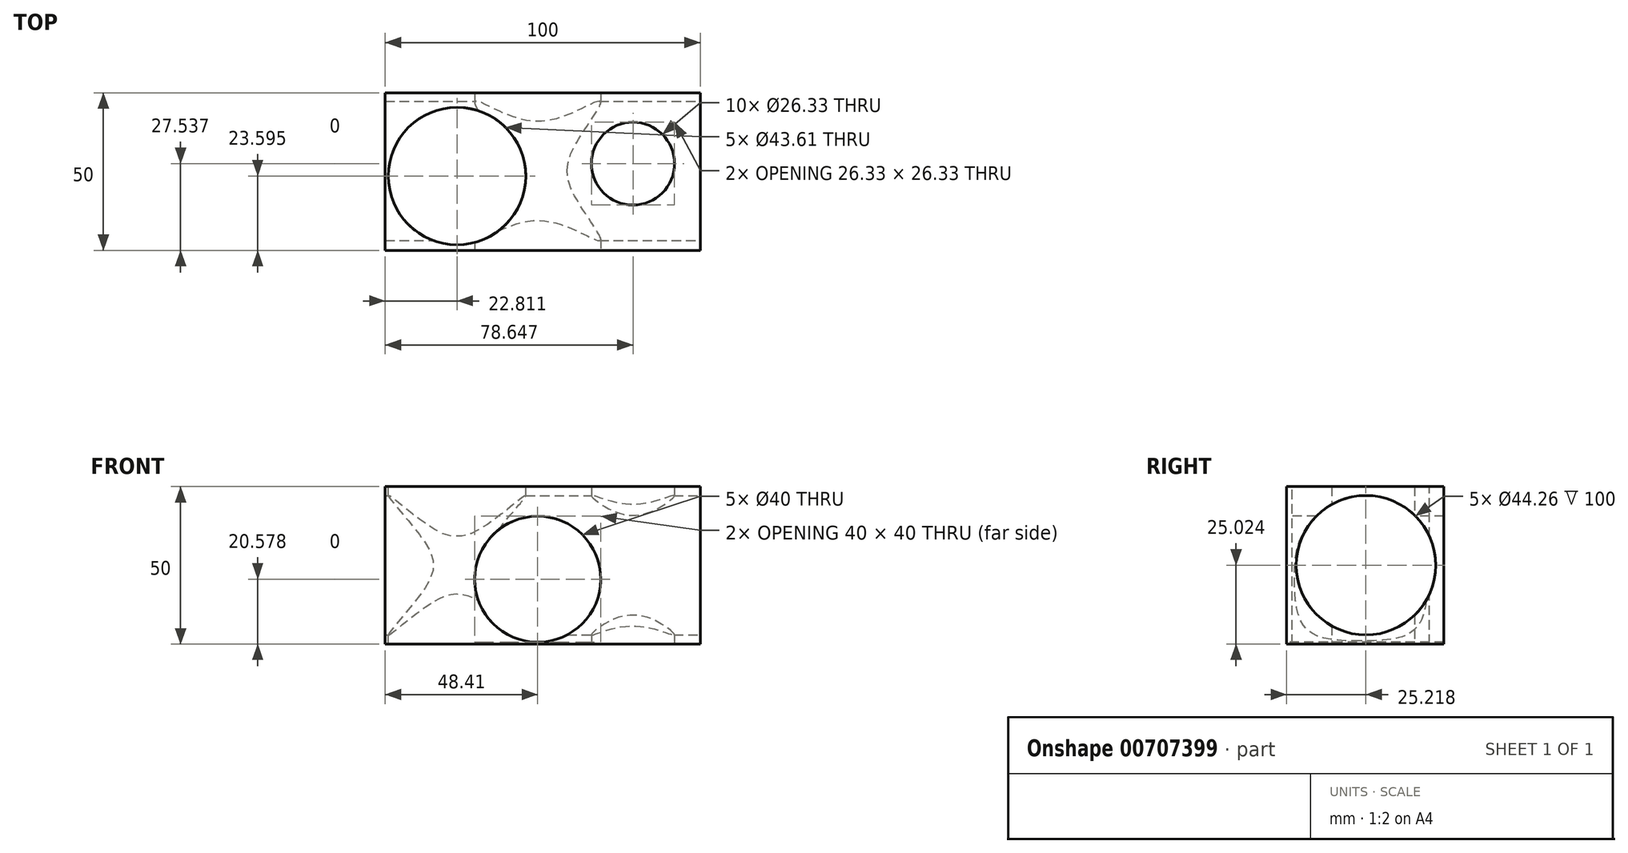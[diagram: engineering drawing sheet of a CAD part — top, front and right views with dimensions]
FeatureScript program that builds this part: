
annotation { "Feature Type Name" : "Feature", "Feature Type Description" : "" }
export const myFeature = defineFeature(function(context is Context, id is Id, definition is map)
    precondition{}
    {
        {
            var Q0;
            Q0=qCreatedBy(makeId("Top.planeOp"),FACE);
            var sketch = newSketch(context, id + "F0", { "sketchPlane" : qUnion([Q0])});
            skLineSegment(sketch, "E0.bottom", {"start": v(-48.41, 7.4) * mm, "end": v(51.59, 7.4) * mm});
            skLineSegment(sketch, "E0.top", {"start": v(-48.41, -42.6) * mm, "end": v(51.59, -42.6) * mm});
            skLineSegment(sketch, "E0.left", {"start": v(-48.41, 7.4) * mm, "end": v(-48.41, -42.6) * mm});
            skLineSegment(sketch, "E0.right", {"start": v(51.59, 7.4) * mm, "end": v(51.59, -42.6) * mm});
            skSolve(sketch);
        }
        {
            var Q0;
            Q0=makeQuery(id+"F0.imprint","IMPRINT",FACE,{"disambiguationData":[TD([[makeQuery(id+"F0.imprint","IMPRINT",EDGE,{"derivedFrom":sQuery(id+"F0.wireOp",EDGE,"E0.bottom")}),-1.0]])]});
            extrude(context, id + "F1", {"entities" : qUnion([Q0]), "depth" : 50 * mm, "offsetDistance" : 25 * mm});
        }
        {
            var Q0;
            Q0=makeQuery(id+"F1.opExtrude","SWEPT_FACE",FACE,{"disambiguationData":[OSD([sQuery(id+"F0.wireOp",EDGE,"E0.top")])]});
            var sketch = newSketch(context, id + "F2", { "sketchPlane" : qUnion([Q0])});
            skCircle(sketch, "E1", {"center": v(0, 20.58) * mm, "radius": 20 * mm});
            skSolve(sketch);
        }
        {
            var Q0;
            Q0=makeQuery(id+"F2.imprint","IMPRINT",FACE,{"disambiguationData":[TD([[makeQuery(id+"F2.imprint","IMPRINT",EDGE,{"derivedFrom":sQuery(id+"F2.wireOp",EDGE,"E1")}),1.0]])]});
            extrude(context, id + "F3", {"entities" : qUnion([Q0]), "operationType" : NewBodyOperationType.REMOVE, "endBound" : BoundingType.UP_TO_NEXT, "oppositeDirection" : true, "depth" : 50 * mm, "offsetDistance" : 25 * mm});
        }
        {
            var Q0;
            Q0=makeQuery(id+"F1.opExtrude","CAP_FACE",FACE,{"disambiguationData":[OSD([sQuery(id+"F0.wireOp",EDGE,"E0.bottom"),sQuery(id+"F0.wireOp",EDGE,"E0.top"),sQuery(id+"F0.wireOp",EDGE,"E0.left"),sQuery(id+"F0.wireOp",EDGE,"E0.right")])],"isStart":true});
            var sketch = newSketch(context, id + "F4", { "sketchPlane" : qUnion([Q0])});
            skCircle(sketch, "E2", {"center": v(30.24, 15.06) * mm, "radius": 13.17 * mm});
            skSolve(sketch);
        }
        {
            var Q0;
            Q0=makeQuery(id+"F4.imprint","IMPRINT",FACE,{"disambiguationData":[TD([[makeQuery(id+"F4.imprint","IMPRINT",EDGE,{"derivedFrom":sQuery(id+"F4.wireOp",EDGE,"E2")}),1.0]])]});
            extrude(context, id + "F5", {"entities" : qUnion([Q0]), "operationType" : NewBodyOperationType.REMOVE, "endBound" : BoundingType.UP_TO_NEXT, "oppositeDirection" : true, "depth" : 50 * mm, "offsetDistance" : 25 * mm});
        }
        {
            var Q0;
            Q0=makeQuery(id+"F1.opExtrude","SWEPT_FACE",FACE,{"disambiguationData":[OSD([sQuery(id+"F0.wireOp",EDGE,"E0.right")])]});
            var sketch = newSketch(context, id + "F6", { "sketchPlane" : qUnion([Q0])});
            skCircle(sketch, "E3", {"center": v(-17.38, 25.02) * mm, "radius": 22.13 * mm});
            skSolve(sketch);
        }
        {
            var Q0;
            Q0=makeQuery(id+"F6.imprint","IMPRINT",FACE,{"disambiguationData":[TD([[makeQuery(id+"F6.imprint","IMPRINT",EDGE,{"derivedFrom":sQuery(id+"F6.wireOp",EDGE,"E3")}),1.0]])]});
            extrude(context, id + "F7", {"entities" : qUnion([Q0]), "operationType" : NewBodyOperationType.REMOVE, "oppositeDirection" : true, "depth" : 100 * mm, "offsetDistance" : 25 * mm});
        }
        {
            var Q0;
            Q0=makeQuery(id+"F1.opExtrude","CAP_FACE",FACE,{"disambiguationData":[OSD([sQuery(id+"F0.wireOp",EDGE,"E0.bottom"),sQuery(id+"F0.wireOp",EDGE,"E0.top"),sQuery(id+"F0.wireOp",EDGE,"E0.left"),sQuery(id+"F0.wireOp",EDGE,"E0.right")])],"isStart":false});
            var sketch = newSketch(context, id + "F8", { "sketchPlane" : qUnion([Q0])});
            skCircle(sketch, "E4", {"center": v(-25.6, -19) * mm, "radius": 21.8 * mm});
            skSolve(sketch);
        }
        {
            var Q0;
            Q0=makeQuery(id+"F8.imprint","IMPRINT",FACE,{"disambiguationData":[TD([[makeQuery(id+"F8.imprint","IMPRINT",EDGE,{"derivedFrom":sQuery(id+"F8.wireOp",EDGE,"E4")}),1.0]])]});
            extrude(context, id + "F9", {"entities" : qUnion([Q0]), "operationType" : NewBodyOperationType.REMOVE, "oppositeDirection" : true, "depth" : 50 * mm, "offsetDistance" : 25 * mm});
        }
    });
